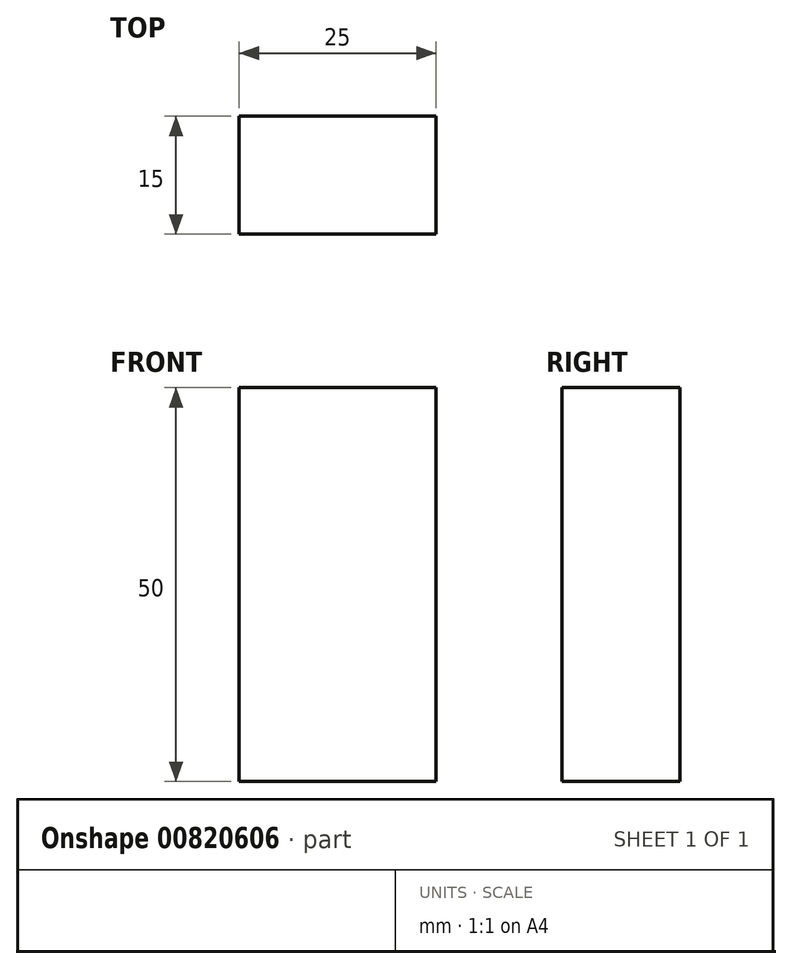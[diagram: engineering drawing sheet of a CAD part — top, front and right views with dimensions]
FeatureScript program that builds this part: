
annotation { "Feature Type Name" : "Feature", "Feature Type Description" : "" }
export const myFeature = defineFeature(function(context is Context, id is Id, definition is map)
    precondition{}
    {
        {
            var Q0;
            Q0=qCreatedBy(makeId("Top.planeOp"),FACE);
            var sketch = newSketch(context, id + "F0", { "sketchPlane" : qUnion([Q0])});
            skLineSegment(sketch, "E0.bottom", {"start": v(-45.47, 40.86) * mm, "end": v(-20.47, 40.86) * mm});
            skLineSegment(sketch, "E0.top", {"start": v(-45.47, 25.86) * mm, "end": v(-20.47, 25.86) * mm});
            skLineSegment(sketch, "E0.left", {"start": v(-45.47, 40.86) * mm, "end": v(-45.47, 25.86) * mm});
            skLineSegment(sketch, "E0.right", {"start": v(-20.47, 40.86) * mm, "end": v(-20.47, 25.86) * mm});
            skSolve(sketch);
        }
        {
            var Q0;
            Q0=qSketchRegion(id+"F0",true);
            extrude(context, id + "F1", {"entities" : qUnion([Q0]), "depth" : 50 * mm, "offsetDistance" : 25 * mm});
        }
    });
